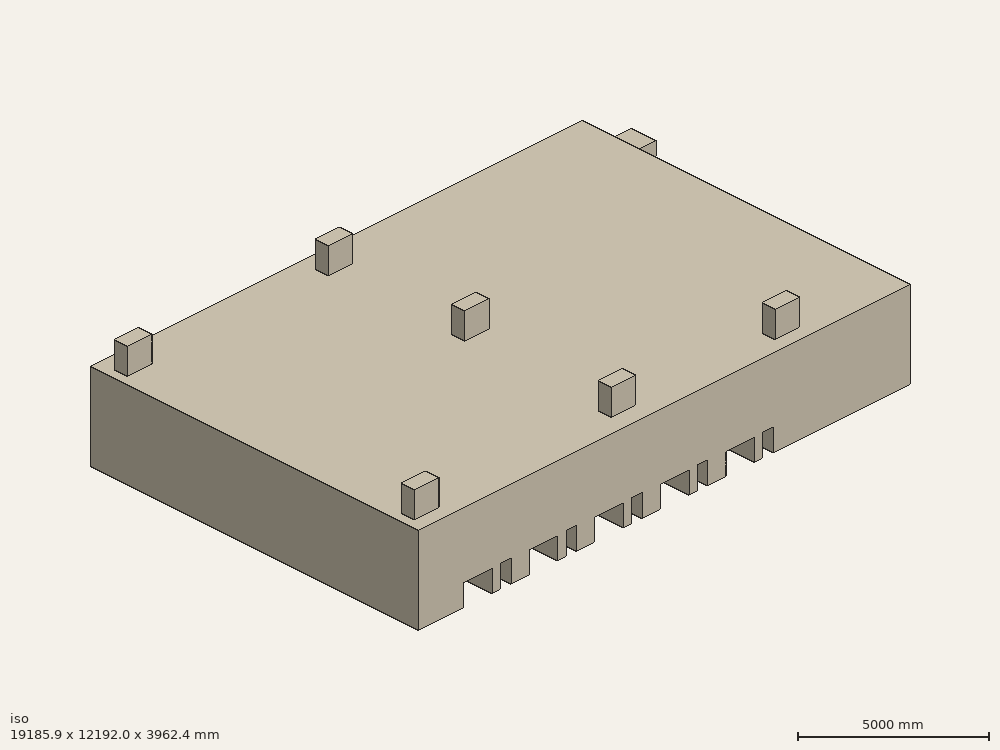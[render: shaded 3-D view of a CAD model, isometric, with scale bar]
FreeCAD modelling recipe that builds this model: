
FCSTD DOCUMENT  (FreeCAD 0.18R14555 (Git shallow))
Label: flow_domain
License: All rights reserved
LicenseURL: http://en.wikipedia.org/wiki/All_rights_reserved
objects: Part::Box×19, Part::MultiFuse×10, Part::Mirroring×1, Part::Cut×1
note: 31 computed .brp shape members not serialized (recipe doc carries the construction recipe); baked Part::Feature solids carry a one-line shape summary decoded from their .brp

FEATURE [Part::Box] Box  label="Room"
  AttacherType = Attacher::AttachEngine3D
  Height = 3048
  Length = 18288
  Width = 12192
FEATURE [Part::Box] Box001  label="Bed 1"
  AttacherType = Attacher::AttachEngine3D
  Height = 762
  Length = 1066.8
  Width = 1981.2
FEATURE [Part::Box] Box002  label="Table 1"
  AttacherType = Attacher::AttachEngine3D
  Height = 798.576
  Length = 396.24
  Placement = pos=(1371.6,0,0) rot=(0,0,1;0rad)
  Width = 396.24
FEATURE [Part::MultiFuse] Fusion  label="Set 1"
  Shapes = -> [Box002,Box001]
FEATURE [Part::Box] Box003  label="Bed 002"
  AttacherType = Attacher::AttachEngine3D
  Height = 762
  Length = 1066.8
  Width = 1981.2
FEATURE [Part::Box] Box004  label="Table 002"
  AttacherType = Attacher::AttachEngine3D
  Height = 798.576
  Length = 396.24
  Placement = pos=(1371.6,0,0) rot=(0,0,1;0rad)
  Width = 396.24
FEATURE [Part::MultiFuse] Fusion001  label="Set 2"
  Placement = pos=(2438.4,0,0) rot=(0,0,1;0rad)
  Shapes = -> [Box004,Box003]
FEATURE [Part::Box] Box005  label="Table 003"
  AttacherType = Attacher::AttachEngine3D
  Height = 798.576
  Length = 396.24
  Placement = pos=(1371.6,0,0) rot=(0,0,1;0rad)
  Width = 396.24
FEATURE [Part::Box] Box006  label="Bed 003"
  AttacherType = Attacher::AttachEngine3D
  Height = 762
  Length = 1066.8
  Width = 1981.2
FEATURE [Part::MultiFuse] Fusion002  label="Set 3"
  Placement = pos=(4876.8,0,0) rot=(0,0,1;0rad)
  Shapes = -> [Box005,Box006]
FEATURE [Part::Box] Box007  label="Bed 004"
  AttacherType = Attacher::AttachEngine3D
  Height = 762
  Length = 1066.8
  Width = 1981.2
FEATURE [Part::Box] Box008  label="Table 004"
  AttacherType = Attacher::AttachEngine3D
  Height = 798.576
  Length = 396.24
  Placement = pos=(1371.6,0,0) rot=(0,0,1;0rad)
  Width = 396.24
FEATURE [Part::MultiFuse] Fusion003  label="Set 4"
  Placement = pos=(7315.2,0,0) rot=(0,0,1;0rad)
  Shapes = -> [Box008,Box007]
FEATURE [Part::Box] Box009  label="Table 005"
  AttacherType = Attacher::AttachEngine3D
  Height = 798.576
  Length = 396.24
  Placement = pos=(1371.6,0,0) rot=(0,0,1;0rad)
  Width = 396.24
FEATURE [Part::Box] Box010  label="Bed 005"
  AttacherType = Attacher::AttachEngine3D
  Height = 762
  Length = 1066.8
  Width = 1981.2
FEATURE [Part::MultiFuse] Fusion004  label="Set 5"
  Placement = pos=(9753.6,0,0) rot=(0,0,1;0rad)
  Shapes = -> [Box009,Box010]
FEATURE [Part::MultiFuse] Fusion005  label="right beds"
  Shapes = -> [Fusion001,Fusion002,Fusion003,Fusion004,Fusion]
FEATURE [Part::Mirroring] Part__Mirroring  label="left beds"
  Base = (0,6096,0)
  Normal = (0,1,0)
  Source = -> Fusion005
FEATURE [Part::Box] Box011  label="Nurse Station"
  AttacherType = Attacher::AttachEngine3D
  Height = 1219.2
  Length = 3048
  Placement = pos=(15240,7620,0) rot=(0,0,1;0rad)
  Width = 4572
FEATURE [Part::Box] Box015  label="Inlet 2"
  AttacherType = Attacher::AttachEngine3D
  Height = 1219.2
  Length = 914.4
  Placement = pos=(13716,457.2,2743.2) rot=(0,0,1;0rad)
  Width = 487.68
FEATURE [Part::Box] Box018  label="Outlet 2"
  AttacherType = Attacher::AttachEngine3D
  Height = 1219.2
  Length = 914.4
  Placement = pos=(304.8,457.2,2743.2) rot=(0,0,1;0rad)
  Width = 487.68
FEATURE [Part::Box] Box019  label="Outlet 1"
  AttacherType = Attacher::AttachEngine3D
  Height = 1219.2
  Length = 914.4
  Placement = pos=(304.8,11125.2,2743.2) rot=(0,0,1;0rad)
  Width = 487.68
FEATURE [Part::MultiFuse] Fusion006  label="all beds"
  Placement = pos=(1676.4,0,0) rot=(0,0,1;0rad)
  Shapes = -> [Part__Mirroring,Fusion005]
FEATURE [Part::MultiFuse] Fusion008  label="surfaces"
  Shapes = -> [Box011,Fusion006]
FEATURE [Part::Box] Box020  label="Outlet 003"
  AttacherType = Attacher::AttachEngine3D
  Height = 1219.2
  Length = 914.4
  Placement = pos=(7772.4,11125.2,2743.2) rot=(0,0,1;0rad)
  Width = 487.68
FEATURE [Part::Box] Box021  label="Outlet 004"
  AttacherType = Attacher::AttachEngine3D
  Height = 1219.2
  Length = 914.4
  Placement = pos=(7772.4,609.6,2743.2) rot=(0,0,1;0rad)
  Width = 487.68
FEATURE [Part::Box] Box022  label="Inlet 003"
  AttacherType = Attacher::AttachEngine3D
  Height = 1219.2
  Length = 914.4
  Placement = pos=(17966.7,10348.6,2324.77) rot=(0.57735,0.57735,0.57735;2.0944rad)
  Width = 487.68
FEATURE [Part::Box] Box023  label="Outlet 005"
  AttacherType = Attacher::AttachEngine3D
  Height = 1219.2
  Length = 914.4
  Placement = pos=(7890.85,6168.42,2743.2) rot=(0,0,1;0rad)
  Width = 487.68
FEATURE [Part::MultiFuse] Fusion009
  Shapes = -> [Box023,Box022,Box020,Box018,Box019,Box015,Box021]
FEATURE [Part::MultiFuse] Fusion010
  Shapes = -> [Fusion009,Box]
FEATURE [Part::Cut] Cut
  Base = -> Fusion010
  Tool = -> Fusion008
